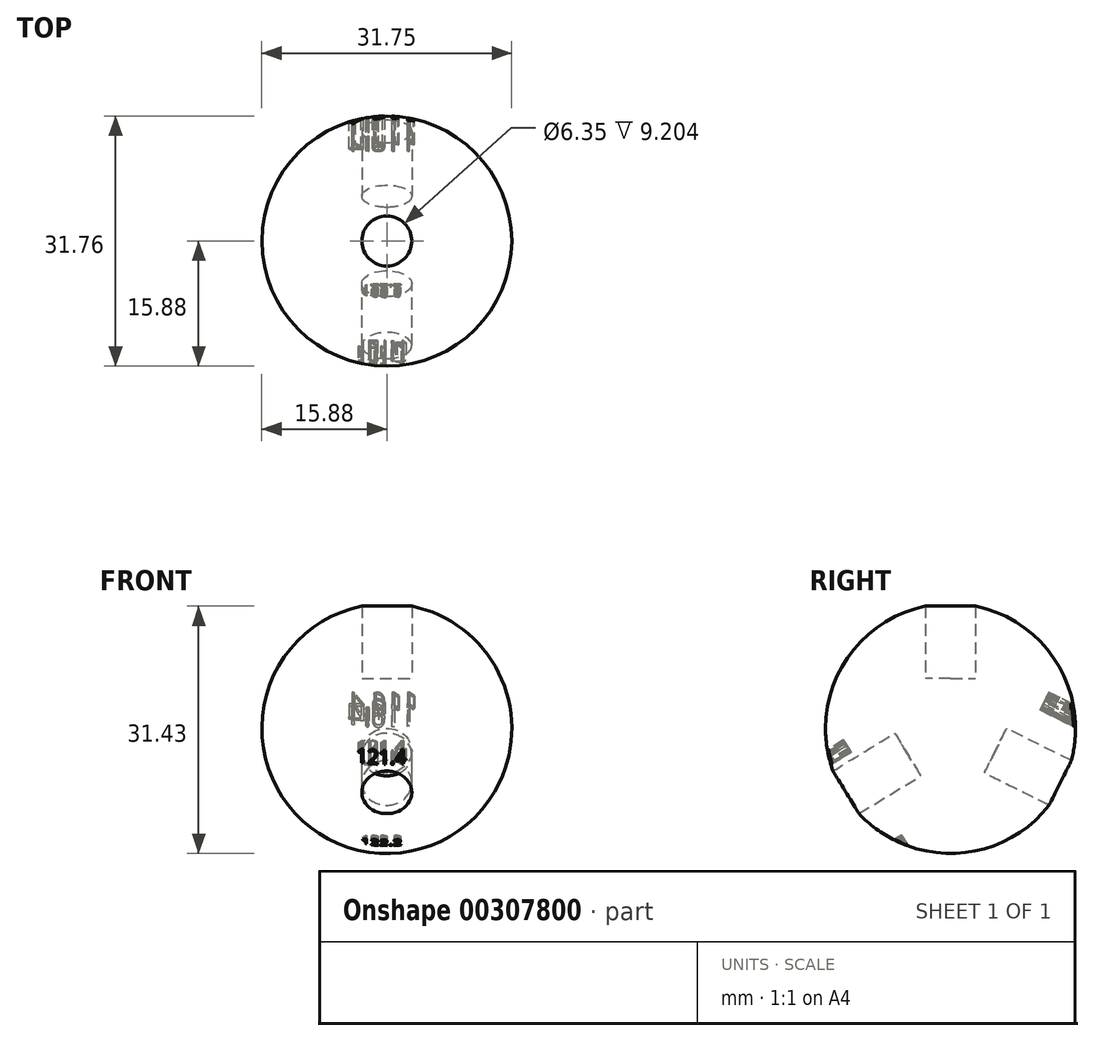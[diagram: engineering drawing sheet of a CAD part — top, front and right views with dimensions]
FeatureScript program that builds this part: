
annotation { "Feature Type Name" : "Feature", "Feature Type Description" : "" }
export const myFeature = defineFeature(function(context is Context, id is Id, definition is map)
    precondition{}
    {
        {
            var Q0;
            Q0=qCreatedBy(makeId("Top.planeOp"),FACE);
            var sketch = newSketch(context, id + "F0", { "sketchPlane" : qUnion([Q0])});
            skArc(sketch, "E0", {"start": v(0, 15.88) * mm, "mid": v(-15.88, 0) * mm, "end": v(0, -15.88) * mm});
            skLineSegment(sketch, "E1", {"start": v(0, 15.88) * mm, "end": v(0, -15.88) * mm});
            skSolve(sketch);
        }
        {
            var Q0;
            Q0=makeQuery(id+"F0.imprint","IMPRINT",FACE,{"disambiguationData":[TD([[makeQuery(id+"F0.imprint","IMPRINT",EDGE,{"derivedFrom":sQuery(id+"F0.wireOp",EDGE,"E0")}),1.0]])]});
            var Q1;
            Q1=sQuery(id+"F0.wireOp",EDGE,"E1");
            revolve(context, id + "F1", {"entities" : qUnion([Q0]), "axis" : qUnion([Q1]), "revolveType" : RevolveType.FULL});
        }
        {
            var Q0;
            Q0=qCreatedBy(makeId("Top.planeOp"),FACE);
            cPlane(context, id + "F2", {"entities" : qUnion([Q0]), "cplaneType" : CPlaneType.OFFSET, "offset" : 6.35 * mm, "width" : 152.4 * mm, "height" : 152.4 * mm});
        }
        {
            var Q0;
            Q0=qCreatedBy(id+"F2.planeOp",FACE);
            var sketch = newSketch(context, id + "F3", { "sketchPlane" : qUnion([Q0])});
            skCircle(sketch, "E2", {"center": v(0, 0) * mm, "radius": 3.18 * mm});
            skSolve(sketch);
        }
        {
            var Q0;
            Q0 = qSketchRegion(id + "F3", true);
            extrude(context, id + "F4", {"entities" : qUnion([Q0]), "depth" : 25.4 * mm});
        }
        {
            var Q0;
            Q0=qCreatedBy(makeId("Front.planeOp"),FACE);
            var sketch = newSketch(context, id + "F5", { "sketchPlane" : qUnion([Q0])});
            skLineSegment(sketch, "E3", {"start": v(0, 0) * mm, "end": v(0, 74.55) * mm, "construction": true});
            skLineSegment(sketch, "E4", {"start": v(0, 0) * mm, "end": v(71.46, 0) * mm, "construction": true});
            skSolve(sketch);
        }
        {
            var Q0;
            Q0=makeQuery(id+"F4.opExtrude","SWEPT_BODY",BODY,{"disambiguationData":[OSD([sQuery(id+"F3.wireOp",EDGE,"E2")])]});
            var Q1;
            Q1=sQuery(id+"F5.wireOp",EDGE,"E4");
            transform(context, id + "F6", {"entities" : qUnion([Q0]), "transformType" : TransformType.ROTATION, "transformAxis" : qUnion([Q1]), "angle" : 121.4 * degree, "makeCopy" : true});
        }
        {
            var Q0;
            Q0=makeQuery(id+"F4.opExtrude","SWEPT_BODY",BODY,{"disambiguationData":[OSD([sQuery(id+"F3.wireOp",EDGE,"E2")])]});
            var Q1;
            Q1=sQuery(id+"F5.wireOp",EDGE,"E4");
            transform(context, id + "F7", {"entities" : qUnion([Q0]), "transformType" : TransformType.ROTATION, "transformAxis" : qUnion([Q1]), "angle" : 116.4 * degree, "oppositeDirection" : true, "makeCopy" : true});
        }
        {
            var Q0;
            Q0=makeQuery(id+"F7.opPattern","COPY",FACE,{"derivedFrom":makeQuery(id+"F4.opExtrude","CAP_FACE",FACE,{"disambiguationData":[OSD([sQuery(id+"F3.wireOp",EDGE,"E2")])],"isStart":false}),"instanceName":"1"});
            cPlane(context, id + "F8", {"entities" : qUnion([Q0]), "cplaneType" : CPlaneType.OFFSET, "offset" : 12.7 * mm, "oppositeDirection" : true, "width" : 152.4 * mm, "height" : 152.4 * mm});
        }
        {
            var Q0;
            Q0=qCreatedBy(id+"F8.planeOp",FACE);
            var sketch = newSketch(context, id + "F9", { "sketchPlane" : qUnion([Q0])});
            skText(sketch, "E5", { "text": "116.4", "fontName": "OpenSans-Regular.ttf"});
            const initialGuessF9  = {"E5": [-0.00383, 0.00722, 1, 0, 0.00245]};
            skSetInitialGuess(sketch, initialGuessF9);
            skSolve(sketch);
        }
        {
            var Q0;
            Q0 = qSketchRegion(id + "F9", true);
            extrude(context, id + "F10", {"entities" : qUnion([Q0]), "operationType" : NewBodyOperationType.REMOVE, "oppositeDirection" : true, "depth" : 9.88 * mm});
        }
        {
            var Q0;
            Q0=makeQuery(id+"F6.opPattern","COPY",FACE,{"derivedFrom":makeQuery(id+"F4.opExtrude","CAP_FACE",FACE,{"disambiguationData":[OSD([sQuery(id+"F3.wireOp",EDGE,"E2")])],"isStart":false}),"instanceName":"1"});
            cPlane(context, id + "F11", {"entities" : qUnion([Q0]), "cplaneType" : CPlaneType.OFFSET, "offset" : 12.7 * mm, "oppositeDirection" : true, "width" : 152.4 * mm, "height" : 152.4 * mm});
        }
        {
            var Q0;
            Q0=qCreatedBy(id+"F11.planeOp",FACE);
            var sketch = newSketch(context, id + "F12", { "sketchPlane" : qUnion([Q0])});
            skText(sketch, "E6", { "text": "121.4", "fontName": "OpenSans-Regular.ttf"});
            skText(sketch, "E7", { "text": "122.2", "fontName": "OpenSans-Regular.ttf"});
            const initialGuessF12  = {"E6": [-0.00385, 0.00403, 1, 0, 0.00178], "E7": [-0.00327, -0.0098, 1, 0, 0.00147]};
            skSetInitialGuess(sketch, initialGuessF12);
            skSolve(sketch);
        }
        {
            var Q0;
            Q0 = qSketchRegion(id + "F12", true);
            extrude(context, id + "F13", {"entities" : qUnion([Q0]), "operationType" : NewBodyOperationType.REMOVE, "oppositeDirection" : true, "depth" : 6.68 * mm});
        }
        {
            var Q0;
            Q0=makeQuery(id+"F4.opExtrude","SWEPT_BODY",BODY,{"disambiguationData":[OSD([sQuery(id+"F3.wireOp",EDGE,"E2")])]});
            var Q1;
            Q1=makeQuery(id+"F6.opPattern","COPY",BODY,{"derivedFrom":makeQuery(id+"F4.opExtrude","SWEPT_BODY",BODY,{"disambiguationData":[OSD([sQuery(id+"F3.wireOp",EDGE,"E2")])]}),"instanceName":"1"});
            var Q2;
            Q2=makeQuery(id+"F7.opPattern","COPY",BODY,{"derivedFrom":makeQuery(id+"F4.opExtrude","SWEPT_BODY",BODY,{"disambiguationData":[OSD([sQuery(id+"F3.wireOp",EDGE,"E2")])]}),"instanceName":"1"});
            var Q3;
            Q3=makeQuery(id+"F1.opRevolve","SWEPT_BODY",BODY,{"disambiguationData":[OSD([sQuery(id+"F0.wireOp",EDGE,"E0"),sQuery(id+"F0.wireOp",EDGE,"E1")])]});
            booleanBodies(context, id + "F14", {"operationType" : BooleanOperationType.SUBTRACTION, "tools" : qUnion([Q0, Q1, Q2]), "targets" : qUnion([Q3])});
        }
    });
